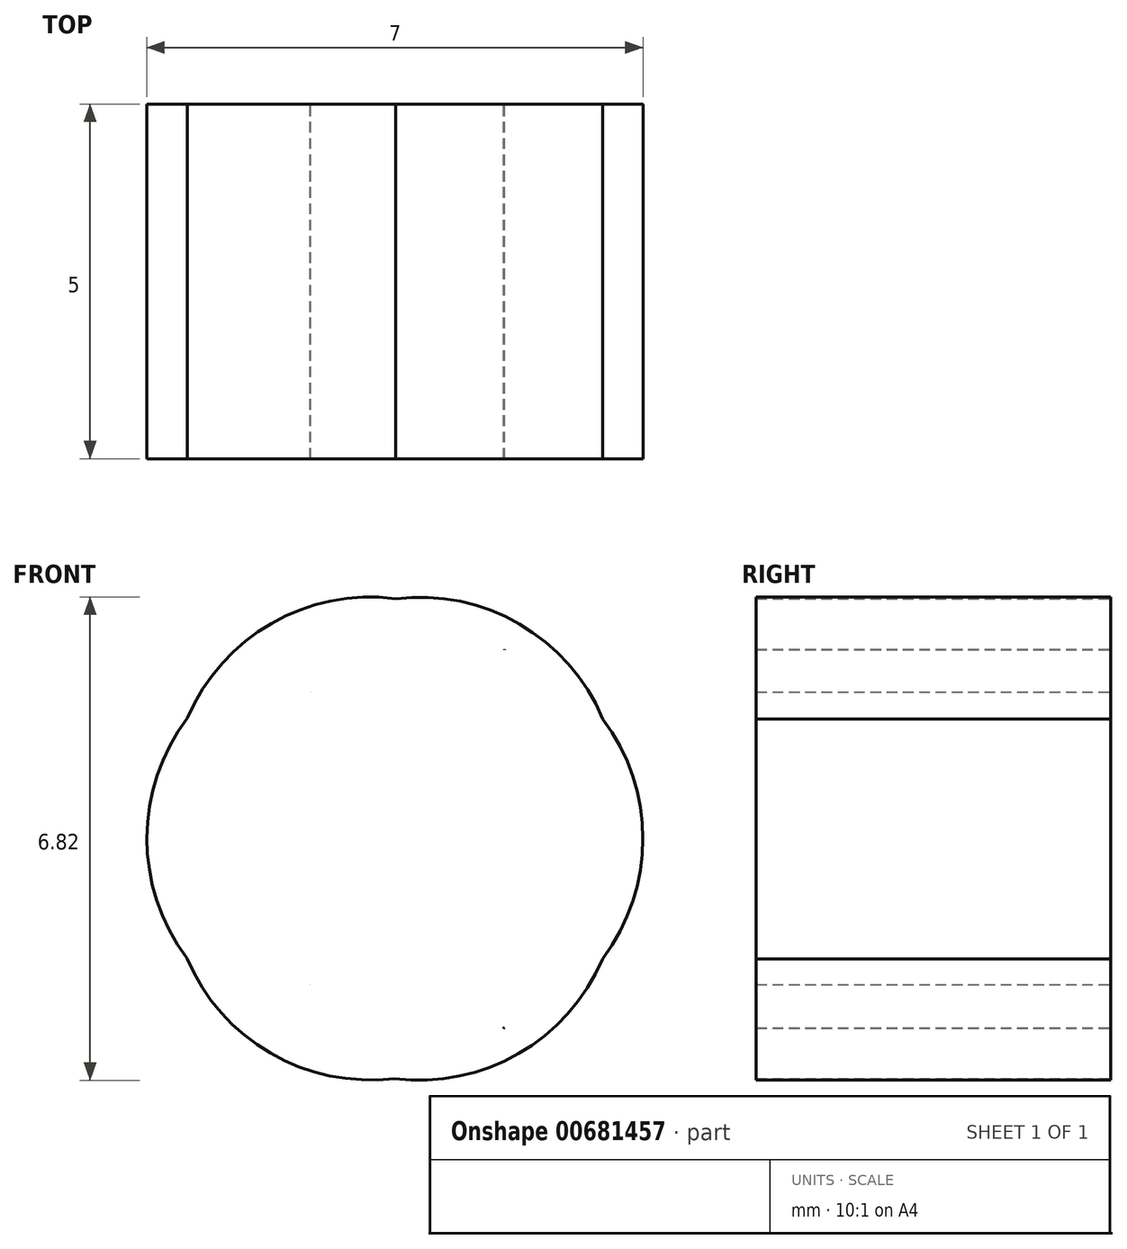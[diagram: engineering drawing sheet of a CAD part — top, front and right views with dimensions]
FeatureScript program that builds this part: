
annotation { "Feature Type Name" : "Feature", "Feature Type Description" : "" }
export const myFeature = defineFeature(function(context is Context, id is Id, definition is map)
    precondition{}
    {
        {
            var Q0;
            Q0=qCreatedBy(makeId("Front.planeOp"),FACE);
            var sketch = newSketch(context, id + "F0", { "sketchPlane" : qUnion([Q0])});
            skCircle(sketch, "E0", {"center": v(0, 0) * mm, "radius": 3.5 * mm});
            skCircle(sketch, "E1.cCircle", {"center": v(0, 0) * mm, "radius": 3.5 * mm, "construction": true});
            skLineSegment(sketch, "E2", {"start": v(1.55, 2.67) * mm, "end": v(1.55, 2.67) * mm});
            skLineSegment(sketch, "E3", {"start": v(-1.2, -2.06) * mm, "end": v(-1.2, -2.06) * mm});
            skLineSegment(sketch, "E4", {"start": v(1.54, -2.67) * mm, "end": v(1.53, -2.67) * mm});
            skArc(sketch, "E5", {"start": v(2.93, 1.69) * mm, "mid": v(1.76, 3.03) * mm, "end": v(0, 3.38) * mm});
            skArc(sketch, "E6", {"start": v(-1.2, -2.06) * mm, "mid": v(-1.2, -2.06) * mm, "end": v(-1.2, -2.06) * mm});
            skArc(sketch, "E7", {"start": v(-1.19, 2.07) * mm, "mid": v(-1.19, 2.07) * mm, "end": v(-1.19, 2.07) * mm});
            skArc(sketch, "E8", {"start": v(0, -3.38) * mm, "mid": v(1.74, -3.03) * mm, "end": v(2.93, -1.7) * mm});
            skArc(sketch, "E9", {"start": v(1.53, -2.67) * mm, "mid": v(1.54, -2.67) * mm, "end": v(1.54, -2.67) * mm});
            skArc(sketch, "E10.trimOffspring", {"start": v(1.55, 2.67) * mm, "mid": v(1.55, 2.67) * mm, "end": v(1.55, 2.67) * mm});
            skLineSegment(sketch, "E11.trimOffspring", {"start": v(-1.19, 2.07) * mm, "end": v(-1.19, 2.07) * mm});
            skPoint(sketch, "E12.start.orphan", {"position": v(3.5, 0) * mm});
            skArc(sketch, "E13.trimOffspring", {"start": v(-2.93, 1.7) * mm, "mid": v(-3.5, 0) * mm, "end": v(-2.93, -1.69) * mm});
            skArc(sketch, "E14.trimOffspring", {"start": v(1.54, -2.67) * mm, "mid": v(1.54, -2.67) * mm, "end": v(1.54, -2.67) * mm});
            skArc(sketch, "E15.trimOffspring", {"start": v(2.93, -1.7) * mm, "mid": v(3.5, 0) * mm, "end": v(2.93, 1.69) * mm});
            skArc(sketch, "E16.trimOffspring", {"start": v(0, 3.38) * mm, "mid": v(-1.74, 3.04) * mm, "end": v(-2.93, 1.7) * mm});
            skArc(sketch, "E17.trimOffspring", {"start": v(-2.93, -1.69) * mm, "mid": v(-1.76, -3.03) * mm, "end": v(0, -3.38) * mm});
            skSolve(sketch);
        }
        {
            var Q0;
            Q0=makeQuery(id+"F0.imprint","IMPRINT",FACE,{"disambiguationData":[TD([[makeQuery(id+"F0.imprint","IMPRINT",EDGE,{"derivedFrom":sQuery(id+"F0.wireOp",EDGE,"E2")}),1.0]])]});
            extrude(context, id + "F1", {"entities" : qUnion([Q0]), "depth" : 5 * mm, "offsetDistance" : 25 * mm});
        }
    });
